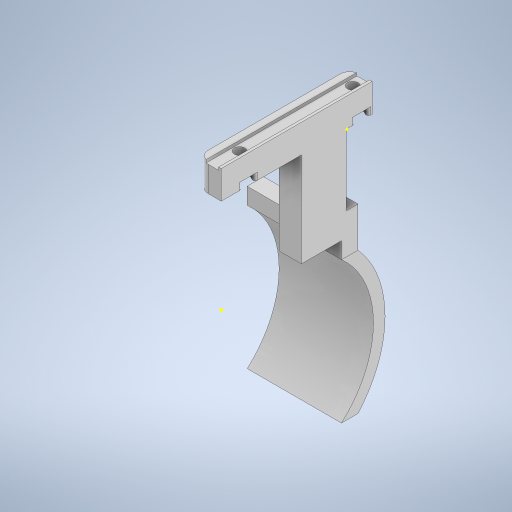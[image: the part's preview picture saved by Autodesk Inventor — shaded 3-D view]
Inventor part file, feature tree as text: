
AUTODESK INVENTOR PART (.ipt)
format: ipt  version: 2024 (Build 280153000, 153)  size: 376,832 bytes
history: native  units: in
note: dims shown in document units (in); Inventor stores cm internally (conversion verified against a paired STEP export)
features: sketch x12, extrude x8, projected_geometry x4, fillet x2, sweep x1
ambient origin geometry x8: Origin, YZ Plane, XZ Plane, XY Plane, X Axis, Y Axis, Z Axis, Center Point
bodies: Solid1 (feature_tree), Solid2 (feature_tree)
feature tree (27):
  extrude  "Extrusion1"  Depth=2.5197in
  extrude  "Extrusion2"  Depth=1.8898in
  extrude  "Extrusion3"  Depth=0.4724in TaperAngle=0.0deg
  fillet  "Fillet1"  Radius=0.0433in
  fillet  "Fillet2"  Radius=0.2126in
  extrude  "Extrusion19"  Depth=0.4724in TaperAngle=0.0deg
  extrude  "Extrusion21"  Depth=0.1181in TaperAngle=0.0deg
  sketch  "Sketch41"  dims[d17=0.1772in d18=0.0394in]
  extrude  "Extrusion22"  Depth=0.0394in
  extrude  "Extrusion25"  Depth=0.4724in
  sweep  "Sweep4"
  extrude  "Extrusion26"  Depth=0.1969in
  sketch  "Sketch60"  dims[d134=1.2008in d135=180.0deg d136=0.2756in d137=1.5748in d138=0.2756in d139=0.2756in d140=0.0in d154=4.1063in d155=0.0in d164=2.3622in d165=1.5748in d166=0.0in d167=0.0in d168=2.4813in d169=0.0in d42=0.0197in d43=0.0344in d44=0.0197in d45=0.0344in d46=0.0in d47=0.0in d48=0.0in d49=0.0in d50=0.0in d51=0.0in d52=0.0in d53=0.0in d55=0.0197in d56=0.0344in d57=0.0197in d58=0.0344in d60=0.0197in d61=0.0344in d62=0.0197in d63=0.0344in d72=0.0197in d73=0.0344in d74=0.0197in d75=0.0344in]
  sketch  "Sketch1"  dims[d1=0.374in d2=2.5197in]
  sketch  "Sketch2"  dims[d3=0.1772in d4=1.8898in]
  sketch  "Sketch3"  dims[d6=0.1457in d7=0.4724in d8=0.0in d9=0.0433in d10=0.2126in]
  projected_geometry  "Projected Loop2"
  projected_geometry  "Projected Loop3"
  projected_geometry  "Projected Loop4"
  projected_geometry  "Projected Loop5"
  sketch  "Sketch28"  dims[d11=0.0472in d12=0.4724in d13=0.0in]
  sketch  "Sketch40"  dims[d14=0.2953in d15=0.1181in d16=0.0in]
  sketch  "Sketch42"  dims[d19=0.1575in d76=0.4724in]
  sketch  "Sketch54"  dims[d107=0.102in d108=0.748in]
  sketch  "Sketch56"  dims[d109=1.1811in d110=0.0in d130=0.1969in]
  sketch  "Sketch58"  dims[d131=0.9449in]
  sketch  "Sketch59"  dims[d132=0.3937in d133=0.0in]
